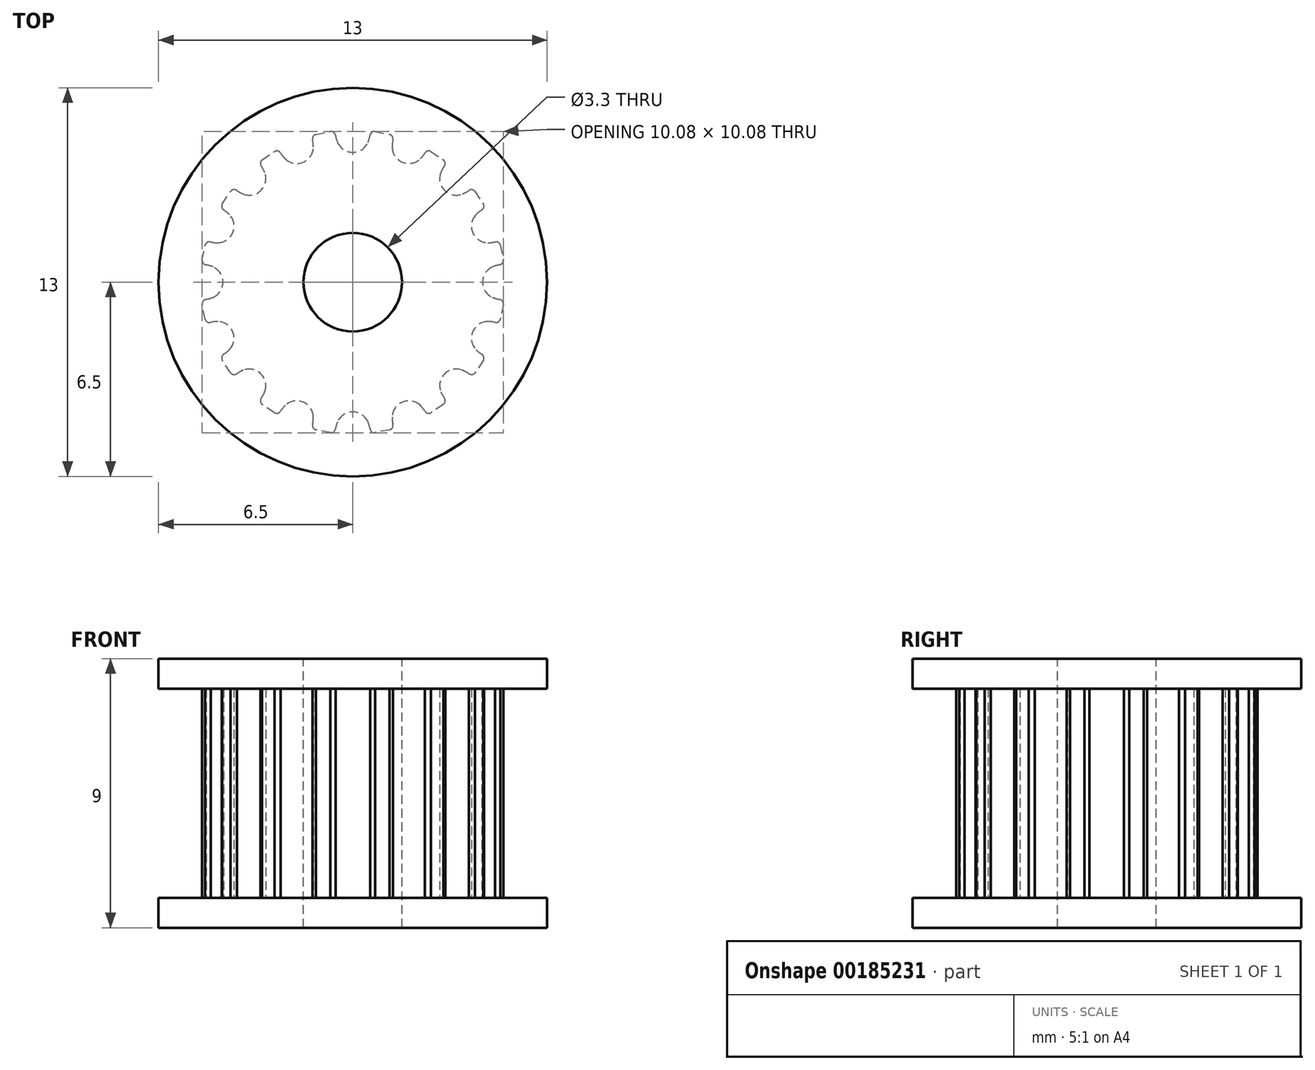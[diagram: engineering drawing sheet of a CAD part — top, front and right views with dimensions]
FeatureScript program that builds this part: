
annotation { "Feature Type Name" : "Feature", "Feature Type Description" : "" }
export const myFeature = defineFeature(function(context is Context, id is Id, definition is map)
    precondition{}
    {
        {
            var Q0;
            Q0=qCreatedBy(makeId("Top.planeOp"),FACE);
            var sketch = newSketch(context, id + "F0", { "sketchPlane" : qUnion([Q0])});
            skLineSegment(sketch, "E0", {"start": v(0, 0) * mm, "end": v(8.05, 0) * mm, "construction": true});
            skArc(sketch, "E1", {"start": v(5.1, 0) * mm, "mid": v(5, 1) * mm, "end": v(4.7, 1.95) * mm, "construction": true});
            skLineSegment(sketch, "E2", {"start": v(0, 0) * mm, "end": v(4.7, 1.95) * mm, "construction": true});
            skPoint(sketch, "E3", {"position": v(4.34, 0) * mm});
            skPoint(sketch, "E4", {"position": v(4.9, 0) * mm});
            skArc(sketch, "E5", {"start": v(4.68, 0.5) * mm, "mid": v(4.34, 0) * mm, "end": v(4.68, -0.5) * mm});
            skArc(sketch, "E6", {"start": v(4.9, 0.58) * mm, "mid": v(4.79, 0.55) * mm, "end": v(4.68, 0.5) * mm});
            skArc(sketch, "E7", {"start": v(4.94, 0) * mm, "mid": v(4.85, 0.96) * mm, "end": v(4.57, 1.9) * mm, "construction": true});
            skArc(sketch, "E8", {"start": v(4.9, 0.58) * mm, "mid": v(5, 0.64) * mm, "end": v(5.04, 0.75) * mm});
            skArc(sketch, "E9", {"start": v(4.97, -1.1) * mm, "mid": v(5.06, -0.56) * mm, "end": v(5.1, 0) * mm, "construction": true});
            skLineSegment(sketch, "E10", {"start": v(0, 0) * mm, "end": v(5, 1) * mm, "construction": true});
            skPoint(sketch, "E11", {"position": v(5, 1) * mm});
            skArc(sketch, "E12.MirrorCS", {"start": v(4.76, 1.34) * mm, "mid": v(4.87, 1.33) * mm, "end": v(4.94, 1.24) * mm});
            skArc(sketch, "E13.MirrorCS", {"start": v(4.76, 1.34) * mm, "mid": v(4.64, 1.32) * mm, "end": v(4.51, 1.32) * mm});
            skArc(sketch, "E14.MirrorCS", {"start": v(4.51, 1.32) * mm, "mid": v(4.01, 1.66) * mm, "end": v(4.12, 2.26) * mm});
            skLineSegment(sketch, "E15", {"start": v(4.94, 1.24) * mm, "end": v(5.04, 0.75) * mm});
            skArc(sketch, "E16.1.0", {"start": v(4.12, 2.26) * mm, "mid": v(4.01, 1.66) * mm, "end": v(4.51, 1.32) * mm});
            skArc(sketch, "E16.1.1", {"start": v(4.31, 2.41) * mm, "mid": v(4.21, 2.34) * mm, "end": v(4.12, 2.26) * mm});
            skArc(sketch, "E16.1.2", {"start": v(4.31, 2.41) * mm, "mid": v(4.38, 2.5) * mm, "end": v(4.37, 2.62) * mm});
            skLineSegment(sketch, "E16.1.3", {"start": v(4.1, 3.03) * mm, "end": v(4.37, 2.62) * mm});
            skArc(sketch, "E16.1.4", {"start": v(3.88, 3.06) * mm, "mid": v(4, 3.1) * mm, "end": v(4.1, 3.03) * mm});
            skArc(sketch, "E16.1.5", {"start": v(3.88, 3.06) * mm, "mid": v(3.78, 3) * mm, "end": v(3.67, 2.95) * mm});
            skArc(sketch, "E16.2.0", {"start": v(2.95, 3.67) * mm, "mid": v(3.07, 3.07) * mm, "end": v(3.67, 2.95) * mm});
            skArc(sketch, "E16.2.1", {"start": v(3.06, 3.88) * mm, "mid": v(3, 3.78) * mm, "end": v(2.95, 3.67) * mm});
            skArc(sketch, "E16.2.2", {"start": v(3.06, 3.88) * mm, "mid": v(3.1, 4) * mm, "end": v(3.03, 4.1) * mm});
            skLineSegment(sketch, "E16.2.3", {"start": v(2.62, 4.37) * mm, "end": v(3.03, 4.1) * mm});
            skArc(sketch, "E16.2.4", {"start": v(2.41, 4.31) * mm, "mid": v(2.5, 4.38) * mm, "end": v(2.62, 4.37) * mm});
            skArc(sketch, "E16.2.5", {"start": v(2.41, 4.31) * mm, "mid": v(2.34, 4.21) * mm, "end": v(2.26, 4.12) * mm});
            skArc(sketch, "E16.3.0", {"start": v(1.32, 4.51) * mm, "mid": v(1.66, 4.01) * mm, "end": v(2.26, 4.12) * mm});
            skArc(sketch, "E16.3.1", {"start": v(1.34, 4.76) * mm, "mid": v(1.32, 4.64) * mm, "end": v(1.32, 4.51) * mm});
            skArc(sketch, "E16.3.2", {"start": v(1.34, 4.76) * mm, "mid": v(1.33, 4.87) * mm, "end": v(1.24, 4.94) * mm});
            skLineSegment(sketch, "E16.3.3", {"start": v(0.75, 5.04) * mm, "end": v(1.24, 4.94) * mm});
            skArc(sketch, "E16.3.4", {"start": v(0.58, 4.9) * mm, "mid": v(0.64, 5) * mm, "end": v(0.75, 5.04) * mm});
            skArc(sketch, "E16.3.5", {"start": v(0.58, 4.9) * mm, "mid": v(0.55, 4.79) * mm, "end": v(0.5, 4.68) * mm});
            skArc(sketch, "E16.4.0", {"start": v(-0.5, 4.68) * mm, "mid": v(0, 4.34) * mm, "end": v(0.5, 4.68) * mm});
            skArc(sketch, "E16.4.1", {"start": v(-0.58, 4.9) * mm, "mid": v(-0.55, 4.79) * mm, "end": v(-0.5, 4.68) * mm});
            skArc(sketch, "E16.4.2", {"start": v(-0.58, 4.9) * mm, "mid": v(-0.64, 5) * mm, "end": v(-0.75, 5.04) * mm});
            skLineSegment(sketch, "E16.4.3", {"start": v(-1.24, 4.94) * mm, "end": v(-0.75, 5.04) * mm});
            skArc(sketch, "E16.4.4", {"start": v(-1.34, 4.76) * mm, "mid": v(-1.33, 4.87) * mm, "end": v(-1.24, 4.94) * mm});
            skArc(sketch, "E16.4.5", {"start": v(-1.34, 4.76) * mm, "mid": v(-1.32, 4.64) * mm, "end": v(-1.32, 4.51) * mm});
            skArc(sketch, "E16.5.0", {"start": v(-2.26, 4.12) * mm, "mid": v(-1.66, 4.01) * mm, "end": v(-1.32, 4.51) * mm});
            skArc(sketch, "E16.5.1", {"start": v(-2.41, 4.31) * mm, "mid": v(-2.34, 4.21) * mm, "end": v(-2.26, 4.12) * mm});
            skArc(sketch, "E16.5.2", {"start": v(-2.41, 4.31) * mm, "mid": v(-2.5, 4.38) * mm, "end": v(-2.62, 4.37) * mm});
            skLineSegment(sketch, "E16.5.3", {"start": v(-3.03, 4.1) * mm, "end": v(-2.62, 4.37) * mm});
            skArc(sketch, "E16.5.4", {"start": v(-3.06, 3.88) * mm, "mid": v(-3.1, 4) * mm, "end": v(-3.03, 4.1) * mm});
            skArc(sketch, "E16.5.5", {"start": v(-3.06, 3.88) * mm, "mid": v(-3, 3.78) * mm, "end": v(-2.95, 3.67) * mm});
            skArc(sketch, "E16.6.0", {"start": v(-3.67, 2.95) * mm, "mid": v(-3.07, 3.07) * mm, "end": v(-2.95, 3.67) * mm});
            skArc(sketch, "E16.6.1", {"start": v(-3.88, 3.06) * mm, "mid": v(-3.78, 3) * mm, "end": v(-3.67, 2.95) * mm});
            skArc(sketch, "E16.6.2", {"start": v(-3.88, 3.06) * mm, "mid": v(-4, 3.1) * mm, "end": v(-4.1, 3.03) * mm});
            skLineSegment(sketch, "E16.6.3", {"start": v(-4.37, 2.62) * mm, "end": v(-4.1, 3.03) * mm});
            skArc(sketch, "E16.6.4", {"start": v(-4.31, 2.41) * mm, "mid": v(-4.38, 2.5) * mm, "end": v(-4.37, 2.62) * mm});
            skArc(sketch, "E16.6.5", {"start": v(-4.31, 2.41) * mm, "mid": v(-4.21, 2.34) * mm, "end": v(-4.12, 2.26) * mm});
            skArc(sketch, "E16.7.0", {"start": v(-4.51, 1.32) * mm, "mid": v(-4.01, 1.66) * mm, "end": v(-4.12, 2.26) * mm});
            skArc(sketch, "E16.7.1", {"start": v(-4.76, 1.34) * mm, "mid": v(-4.64, 1.32) * mm, "end": v(-4.51, 1.32) * mm});
            skArc(sketch, "E16.7.2", {"start": v(-4.76, 1.34) * mm, "mid": v(-4.87, 1.33) * mm, "end": v(-4.94, 1.24) * mm});
            skLineSegment(sketch, "E16.7.3", {"start": v(-5.04, 0.75) * mm, "end": v(-4.94, 1.24) * mm});
            skArc(sketch, "E16.7.4", {"start": v(-4.9, 0.58) * mm, "mid": v(-5, 0.64) * mm, "end": v(-5.04, 0.75) * mm});
            skArc(sketch, "E16.7.5", {"start": v(-4.9, 0.58) * mm, "mid": v(-4.79, 0.55) * mm, "end": v(-4.68, 0.5) * mm});
            skArc(sketch, "E16.8.0", {"start": v(-4.68, -0.5) * mm, "mid": v(-4.34, 0) * mm, "end": v(-4.68, 0.5) * mm});
            skArc(sketch, "E16.8.1", {"start": v(-4.9, -0.58) * mm, "mid": v(-4.79, -0.55) * mm, "end": v(-4.68, -0.5) * mm});
            skArc(sketch, "E16.8.2", {"start": v(-4.9, -0.58) * mm, "mid": v(-5, -0.64) * mm, "end": v(-5.04, -0.75) * mm});
            skLineSegment(sketch, "E16.8.3", {"start": v(-4.94, -1.24) * mm, "end": v(-5.04, -0.75) * mm});
            skArc(sketch, "E16.8.4", {"start": v(-4.76, -1.34) * mm, "mid": v(-4.87, -1.33) * mm, "end": v(-4.94, -1.24) * mm});
            skArc(sketch, "E16.8.5", {"start": v(-4.76, -1.34) * mm, "mid": v(-4.64, -1.32) * mm, "end": v(-4.51, -1.32) * mm});
            skArc(sketch, "E16.9.0", {"start": v(-4.12, -2.26) * mm, "mid": v(-4.01, -1.66) * mm, "end": v(-4.51, -1.32) * mm});
            skArc(sketch, "E16.9.1", {"start": v(-4.31, -2.41) * mm, "mid": v(-4.21, -2.34) * mm, "end": v(-4.12, -2.26) * mm});
            skArc(sketch, "E16.9.2", {"start": v(-4.31, -2.41) * mm, "mid": v(-4.38, -2.5) * mm, "end": v(-4.37, -2.62) * mm});
            skLineSegment(sketch, "E16.9.3", {"start": v(-4.1, -3.03) * mm, "end": v(-4.37, -2.62) * mm});
            skArc(sketch, "E16.9.4", {"start": v(-3.88, -3.06) * mm, "mid": v(-4, -3.1) * mm, "end": v(-4.1, -3.03) * mm});
            skArc(sketch, "E16.9.5", {"start": v(-3.88, -3.06) * mm, "mid": v(-3.78, -3) * mm, "end": v(-3.67, -2.95) * mm});
            skArc(sketch, "E16.10.0", {"start": v(-2.95, -3.67) * mm, "mid": v(-3.07, -3.07) * mm, "end": v(-3.67, -2.95) * mm});
            skArc(sketch, "E16.10.1", {"start": v(-3.06, -3.88) * mm, "mid": v(-3, -3.78) * mm, "end": v(-2.95, -3.67) * mm});
            skArc(sketch, "E16.10.2", {"start": v(-3.06, -3.88) * mm, "mid": v(-3.1, -4) * mm, "end": v(-3.03, -4.1) * mm});
            skLineSegment(sketch, "E16.10.3", {"start": v(-2.62, -4.37) * mm, "end": v(-3.03, -4.1) * mm});
            skArc(sketch, "E16.10.4", {"start": v(-2.41, -4.31) * mm, "mid": v(-2.5, -4.38) * mm, "end": v(-2.62, -4.37) * mm});
            skArc(sketch, "E16.10.5", {"start": v(-2.41, -4.31) * mm, "mid": v(-2.34, -4.21) * mm, "end": v(-2.26, -4.12) * mm});
            skArc(sketch, "E16.11.0", {"start": v(-1.32, -4.51) * mm, "mid": v(-1.66, -4.01) * mm, "end": v(-2.26, -4.12) * mm});
            skArc(sketch, "E16.11.1", {"start": v(-1.34, -4.76) * mm, "mid": v(-1.32, -4.64) * mm, "end": v(-1.32, -4.51) * mm});
            skArc(sketch, "E16.11.2", {"start": v(-1.34, -4.76) * mm, "mid": v(-1.33, -4.87) * mm, "end": v(-1.24, -4.94) * mm});
            skLineSegment(sketch, "E16.11.3", {"start": v(-0.75, -5.04) * mm, "end": v(-1.24, -4.94) * mm});
            skArc(sketch, "E16.11.4", {"start": v(-0.58, -4.9) * mm, "mid": v(-0.64, -5) * mm, "end": v(-0.75, -5.04) * mm});
            skArc(sketch, "E16.11.5", {"start": v(-0.58, -4.9) * mm, "mid": v(-0.55, -4.79) * mm, "end": v(-0.5, -4.68) * mm});
            skArc(sketch, "E16.12.0", {"start": v(0.5, -4.68) * mm, "mid": v(0, -4.34) * mm, "end": v(-0.5, -4.68) * mm});
            skArc(sketch, "E16.12.1", {"start": v(0.58, -4.9) * mm, "mid": v(0.55, -4.79) * mm, "end": v(0.5, -4.68) * mm});
            skArc(sketch, "E16.12.2", {"start": v(0.58, -4.9) * mm, "mid": v(0.64, -5) * mm, "end": v(0.75, -5.04) * mm});
            skLineSegment(sketch, "E16.12.3", {"start": v(1.24, -4.94) * mm, "end": v(0.75, -5.04) * mm});
            skArc(sketch, "E16.12.4", {"start": v(1.34, -4.76) * mm, "mid": v(1.33, -4.87) * mm, "end": v(1.24, -4.94) * mm});
            skArc(sketch, "E16.12.5", {"start": v(1.34, -4.76) * mm, "mid": v(1.32, -4.64) * mm, "end": v(1.32, -4.51) * mm});
            skArc(sketch, "E16.13.0", {"start": v(2.26, -4.12) * mm, "mid": v(1.66, -4.01) * mm, "end": v(1.32, -4.51) * mm});
            skArc(sketch, "E16.13.1", {"start": v(2.41, -4.31) * mm, "mid": v(2.34, -4.21) * mm, "end": v(2.26, -4.12) * mm});
            skArc(sketch, "E16.13.2", {"start": v(2.41, -4.31) * mm, "mid": v(2.5, -4.38) * mm, "end": v(2.62, -4.37) * mm});
            skLineSegment(sketch, "E16.13.3", {"start": v(3.03, -4.1) * mm, "end": v(2.62, -4.37) * mm});
            skArc(sketch, "E16.13.4", {"start": v(3.06, -3.88) * mm, "mid": v(3.1, -4) * mm, "end": v(3.03, -4.1) * mm});
            skArc(sketch, "E16.13.5", {"start": v(3.06, -3.88) * mm, "mid": v(3, -3.78) * mm, "end": v(2.95, -3.67) * mm});
            skArc(sketch, "E16.14.0", {"start": v(3.67, -2.95) * mm, "mid": v(3.07, -3.07) * mm, "end": v(2.95, -3.67) * mm});
            skArc(sketch, "E16.14.1", {"start": v(3.88, -3.06) * mm, "mid": v(3.78, -3) * mm, "end": v(3.67, -2.95) * mm});
            skArc(sketch, "E16.14.2", {"start": v(3.88, -3.06) * mm, "mid": v(4, -3.1) * mm, "end": v(4.1, -3.03) * mm});
            skLineSegment(sketch, "E16.14.3", {"start": v(4.37, -2.62) * mm, "end": v(4.1, -3.03) * mm});
            skArc(sketch, "E16.14.4", {"start": v(4.31, -2.41) * mm, "mid": v(4.38, -2.5) * mm, "end": v(4.37, -2.62) * mm});
            skArc(sketch, "E16.14.5", {"start": v(4.31, -2.41) * mm, "mid": v(4.21, -2.34) * mm, "end": v(4.12, -2.26) * mm});
            skArc(sketch, "E16.15.0", {"start": v(4.51, -1.32) * mm, "mid": v(4.01, -1.66) * mm, "end": v(4.12, -2.26) * mm});
            skArc(sketch, "E16.15.1", {"start": v(4.76, -1.34) * mm, "mid": v(4.64, -1.32) * mm, "end": v(4.51, -1.32) * mm});
            skArc(sketch, "E16.15.2", {"start": v(4.76, -1.34) * mm, "mid": v(4.87, -1.33) * mm, "end": v(4.94, -1.24) * mm});
            skLineSegment(sketch, "E16.15.3", {"start": v(5.04, -0.75) * mm, "end": v(4.94, -1.24) * mm});
            skArc(sketch, "E16.15.4", {"start": v(4.9, -0.58) * mm, "mid": v(5, -0.64) * mm, "end": v(5.04, -0.75) * mm});
            skArc(sketch, "E16.15.5", {"start": v(4.9, -0.58) * mm, "mid": v(4.79, -0.55) * mm, "end": v(4.68, -0.5) * mm});
            skCircle(sketch, "E17", {"center": v(0, 0) * mm, "radius": 1.65 * mm});
            skCircle(sketch, "E18", {"center": v(0, 0) * mm, "radius": 6.5 * mm});
            skSolve(sketch);
        }
        {
            var Q0;
            Q0=makeQuery(id+"F0.imprint","IMPRINT",FACE,{"disambiguationData":[TD([[makeQuery(id+"F0.imprint","IMPRINT",EDGE,{"derivedFrom":sQuery(id+"F0.wireOp",EDGE,"E5")}),-1.0]])]});
            var Q1;
            Q1=makeQuery(id+"F0.imprint","IMPRINT",FACE,{"disambiguationData":[TD([[makeQuery(id+"F0.imprint","IMPRINT",EDGE,{"derivedFrom":sQuery(id+"F0.wireOp",EDGE,"E5")}),1.0]])]});
            extrude(context, id + "F1", {"entities" : qUnion([Q0, Q1]), "oppositeDirection" : true, "depth" : 1 * mm});
        }
        {
            var Q0;
            Q0=makeQuery(id+"F0.imprint","IMPRINT",FACE,{"disambiguationData":[TD([[makeQuery(id+"F0.imprint","IMPRINT",EDGE,{"derivedFrom":sQuery(id+"F0.wireOp",EDGE,"E5")}),-1.0]])]});
            extrude(context, id + "F2", {"entities" : qUnion([Q0]), "operationType" : NewBodyOperationType.ADD, "depth" : 7 * mm});
        }
        {
            var Q0;
            Q0=makeQuery(id+"F0.imprint","IMPRINT",FACE,{"disambiguationData":[TD([[makeQuery(id+"F0.imprint","IMPRINT",EDGE,{"derivedFrom":sQuery(id+"F0.wireOp",EDGE,"E5")}),1.0]])]});
            var Q1;
            Q1=makeQuery(id+"F0.imprint","IMPRINT",FACE,{"disambiguationData":[TD([[makeQuery(id+"F0.imprint","IMPRINT",EDGE,{"derivedFrom":sQuery(id+"F0.wireOp",EDGE,"E5")}),-1.0]])]});
            var Q2;
            Q2=makeQuery(id+"F2.opExtrude","CAP_FACE",FACE,{"disambiguationData":[OSD([sQuery(id+"F0.wireOp",EDGE,"E5"),sQuery(id+"F0.wireOp",EDGE,"E6"),sQuery(id+"F0.wireOp",EDGE,"E8"),sQuery(id+"F0.wireOp",EDGE,"E12.MirrorCS"),sQuery(id+"F0.wireOp",EDGE,"E13.MirrorCS"),sQuery(id+"F0.wireOp",EDGE,"E15"),sQuery(id+"F0.wireOp",EDGE,"E16.1.0"),sQuery(id+"F0.wireOp",EDGE,"E16.1.1"),sQuery(id+"F0.wireOp",EDGE,"E16.1.2"),sQuery(id+"F0.wireOp",EDGE,"E16.1.3"),sQuery(id+"F0.wireOp",EDGE,"E16.1.4"),sQuery(id+"F0.wireOp",EDGE,"E16.1.5"),sQuery(id+"F0.wireOp",EDGE,"E16.2.0"),sQuery(id+"F0.wireOp",EDGE,"E16.2.1"),sQuery(id+"F0.wireOp",EDGE,"E16.2.2"),sQuery(id+"F0.wireOp",EDGE,"E16.2.3"),sQuery(id+"F0.wireOp",EDGE,"E16.2.4"),sQuery(id+"F0.wireOp",EDGE,"E16.2.5"),sQuery(id+"F0.wireOp",EDGE,"E16.3.0"),sQuery(id+"F0.wireOp",EDGE,"E16.3.1"),sQuery(id+"F0.wireOp",EDGE,"E16.3.2"),sQuery(id+"F0.wireOp",EDGE,"E16.3.3"),sQuery(id+"F0.wireOp",EDGE,"E16.3.4"),sQuery(id+"F0.wireOp",EDGE,"E16.3.5"),sQuery(id+"F0.wireOp",EDGE,"E16.4.0"),sQuery(id+"F0.wireOp",EDGE,"E16.4.1"),sQuery(id+"F0.wireOp",EDGE,"E16.4.2"),sQuery(id+"F0.wireOp",EDGE,"E16.4.3"),sQuery(id+"F0.wireOp",EDGE,"E16.4.4"),sQuery(id+"F0.wireOp",EDGE,"E16.4.5"),sQuery(id+"F0.wireOp",EDGE,"E16.5.0"),sQuery(id+"F0.wireOp",EDGE,"E16.5.1"),sQuery(id+"F0.wireOp",EDGE,"E16.5.2"),sQuery(id+"F0.wireOp",EDGE,"E16.5.3"),sQuery(id+"F0.wireOp",EDGE,"E16.5.4"),sQuery(id+"F0.wireOp",EDGE,"E16.5.5"),sQuery(id+"F0.wireOp",EDGE,"E16.6.0"),sQuery(id+"F0.wireOp",EDGE,"E16.6.1"),sQuery(id+"F0.wireOp",EDGE,"E16.6.2"),sQuery(id+"F0.wireOp",EDGE,"E16.6.3"),sQuery(id+"F0.wireOp",EDGE,"E16.6.4"),sQuery(id+"F0.wireOp",EDGE,"E16.6.5"),sQuery(id+"F0.wireOp",EDGE,"E16.7.0"),sQuery(id+"F0.wireOp",EDGE,"E16.7.1"),sQuery(id+"F0.wireOp",EDGE,"E16.7.2"),sQuery(id+"F0.wireOp",EDGE,"E16.7.3"),sQuery(id+"F0.wireOp",EDGE,"E16.7.4"),sQuery(id+"F0.wireOp",EDGE,"E16.7.5"),sQuery(id+"F0.wireOp",EDGE,"E16.8.0"),sQuery(id+"F0.wireOp",EDGE,"E16.8.1"),sQuery(id+"F0.wireOp",EDGE,"E16.8.2"),sQuery(id+"F0.wireOp",EDGE,"E16.8.3"),sQuery(id+"F0.wireOp",EDGE,"E16.8.4"),sQuery(id+"F0.wireOp",EDGE,"E16.8.5"),sQuery(id+"F0.wireOp",EDGE,"E16.9.0"),sQuery(id+"F0.wireOp",EDGE,"E16.9.1"),sQuery(id+"F0.wireOp",EDGE,"E16.9.2"),sQuery(id+"F0.wireOp",EDGE,"E16.9.3"),sQuery(id+"F0.wireOp",EDGE,"E16.9.4"),sQuery(id+"F0.wireOp",EDGE,"E16.9.5"),sQuery(id+"F0.wireOp",EDGE,"E16.10.0"),sQuery(id+"F0.wireOp",EDGE,"E16.10.1"),sQuery(id+"F0.wireOp",EDGE,"E16.10.2"),sQuery(id+"F0.wireOp",EDGE,"E16.10.3"),sQuery(id+"F0.wireOp",EDGE,"E16.10.4"),sQuery(id+"F0.wireOp",EDGE,"E16.10.5"),sQuery(id+"F0.wireOp",EDGE,"E16.11.0"),sQuery(id+"F0.wireOp",EDGE,"E16.11.1"),sQuery(id+"F0.wireOp",EDGE,"E16.11.2"),sQuery(id+"F0.wireOp",EDGE,"E16.11.3"),sQuery(id+"F0.wireOp",EDGE,"E16.11.4"),sQuery(id+"F0.wireOp",EDGE,"E16.11.5"),sQuery(id+"F0.wireOp",EDGE,"E16.12.0"),sQuery(id+"F0.wireOp",EDGE,"E16.12.1"),sQuery(id+"F0.wireOp",EDGE,"E16.12.2"),sQuery(id+"F0.wireOp",EDGE,"E16.12.3"),sQuery(id+"F0.wireOp",EDGE,"E16.12.4"),sQuery(id+"F0.wireOp",EDGE,"E16.12.5"),sQuery(id+"F0.wireOp",EDGE,"E16.13.0"),sQuery(id+"F0.wireOp",EDGE,"E16.13.1"),sQuery(id+"F0.wireOp",EDGE,"E16.13.2"),sQuery(id+"F0.wireOp",EDGE,"E16.13.3"),sQuery(id+"F0.wireOp",EDGE,"E16.13.4"),sQuery(id+"F0.wireOp",EDGE,"E16.13.5"),sQuery(id+"F0.wireOp",EDGE,"E16.14.0"),sQuery(id+"F0.wireOp",EDGE,"E16.14.1"),sQuery(id+"F0.wireOp",EDGE,"E16.14.2"),sQuery(id+"F0.wireOp",EDGE,"E16.14.3"),sQuery(id+"F0.wireOp",EDGE,"E16.14.4"),sQuery(id+"F0.wireOp",EDGE,"E16.14.5"),sQuery(id+"F0.wireOp",EDGE,"E16.15.0"),sQuery(id+"F0.wireOp",EDGE,"E16.15.1"),sQuery(id+"F0.wireOp",EDGE,"E16.15.2"),sQuery(id+"F0.wireOp",EDGE,"E16.15.3"),sQuery(id+"F0.wireOp",EDGE,"E16.15.4"),sQuery(id+"F0.wireOp",EDGE,"E16.15.5"),sQuery(id+"F0.wireOp",EDGE,"E17")])],"isStart":false});
            var Q3;
            Q3=makeQuery(id+"F2.opExtrude","CAP_FACE",FACE,{"disambiguationData":[OSD([sQuery(id+"F0.wireOp",EDGE,"E5"),sQuery(id+"F0.wireOp",EDGE,"E6"),sQuery(id+"F0.wireOp",EDGE,"E8"),sQuery(id+"F0.wireOp",EDGE,"E12.MirrorCS"),sQuery(id+"F0.wireOp",EDGE,"E13.MirrorCS"),sQuery(id+"F0.wireOp",EDGE,"E15"),sQuery(id+"F0.wireOp",EDGE,"E16.1.0"),sQuery(id+"F0.wireOp",EDGE,"E16.1.1"),sQuery(id+"F0.wireOp",EDGE,"E16.1.2"),sQuery(id+"F0.wireOp",EDGE,"E16.1.3"),sQuery(id+"F0.wireOp",EDGE,"E16.1.4"),sQuery(id+"F0.wireOp",EDGE,"E16.1.5"),sQuery(id+"F0.wireOp",EDGE,"E16.2.0"),sQuery(id+"F0.wireOp",EDGE,"E16.2.1"),sQuery(id+"F0.wireOp",EDGE,"E16.2.2"),sQuery(id+"F0.wireOp",EDGE,"E16.2.3"),sQuery(id+"F0.wireOp",EDGE,"E16.2.4"),sQuery(id+"F0.wireOp",EDGE,"E16.2.5"),sQuery(id+"F0.wireOp",EDGE,"E16.3.0"),sQuery(id+"F0.wireOp",EDGE,"E16.3.1"),sQuery(id+"F0.wireOp",EDGE,"E16.3.2"),sQuery(id+"F0.wireOp",EDGE,"E16.3.3"),sQuery(id+"F0.wireOp",EDGE,"E16.3.4"),sQuery(id+"F0.wireOp",EDGE,"E16.3.5"),sQuery(id+"F0.wireOp",EDGE,"E16.4.0"),sQuery(id+"F0.wireOp",EDGE,"E16.4.1"),sQuery(id+"F0.wireOp",EDGE,"E16.4.2"),sQuery(id+"F0.wireOp",EDGE,"E16.4.3"),sQuery(id+"F0.wireOp",EDGE,"E16.4.4"),sQuery(id+"F0.wireOp",EDGE,"E16.4.5"),sQuery(id+"F0.wireOp",EDGE,"E16.5.0"),sQuery(id+"F0.wireOp",EDGE,"E16.5.1"),sQuery(id+"F0.wireOp",EDGE,"E16.5.2"),sQuery(id+"F0.wireOp",EDGE,"E16.5.3"),sQuery(id+"F0.wireOp",EDGE,"E16.5.4"),sQuery(id+"F0.wireOp",EDGE,"E16.5.5"),sQuery(id+"F0.wireOp",EDGE,"E16.6.0"),sQuery(id+"F0.wireOp",EDGE,"E16.6.1"),sQuery(id+"F0.wireOp",EDGE,"E16.6.2"),sQuery(id+"F0.wireOp",EDGE,"E16.6.3"),sQuery(id+"F0.wireOp",EDGE,"E16.6.4"),sQuery(id+"F0.wireOp",EDGE,"E16.6.5"),sQuery(id+"F0.wireOp",EDGE,"E16.7.0"),sQuery(id+"F0.wireOp",EDGE,"E16.7.1"),sQuery(id+"F0.wireOp",EDGE,"E16.7.2"),sQuery(id+"F0.wireOp",EDGE,"E16.7.3"),sQuery(id+"F0.wireOp",EDGE,"E16.7.4"),sQuery(id+"F0.wireOp",EDGE,"E16.7.5"),sQuery(id+"F0.wireOp",EDGE,"E16.8.0"),sQuery(id+"F0.wireOp",EDGE,"E16.8.1"),sQuery(id+"F0.wireOp",EDGE,"E16.8.2"),sQuery(id+"F0.wireOp",EDGE,"E16.8.3"),sQuery(id+"F0.wireOp",EDGE,"E16.8.4"),sQuery(id+"F0.wireOp",EDGE,"E16.8.5"),sQuery(id+"F0.wireOp",EDGE,"E16.9.0"),sQuery(id+"F0.wireOp",EDGE,"E16.9.1"),sQuery(id+"F0.wireOp",EDGE,"E16.9.2"),sQuery(id+"F0.wireOp",EDGE,"E16.9.3"),sQuery(id+"F0.wireOp",EDGE,"E16.9.4"),sQuery(id+"F0.wireOp",EDGE,"E16.9.5"),sQuery(id+"F0.wireOp",EDGE,"E16.10.0"),sQuery(id+"F0.wireOp",EDGE,"E16.10.1"),sQuery(id+"F0.wireOp",EDGE,"E16.10.2"),sQuery(id+"F0.wireOp",EDGE,"E16.10.3"),sQuery(id+"F0.wireOp",EDGE,"E16.10.4"),sQuery(id+"F0.wireOp",EDGE,"E16.10.5"),sQuery(id+"F0.wireOp",EDGE,"E16.11.0"),sQuery(id+"F0.wireOp",EDGE,"E16.11.1"),sQuery(id+"F0.wireOp",EDGE,"E16.11.2"),sQuery(id+"F0.wireOp",EDGE,"E16.11.3"),sQuery(id+"F0.wireOp",EDGE,"E16.11.4"),sQuery(id+"F0.wireOp",EDGE,"E16.11.5"),sQuery(id+"F0.wireOp",EDGE,"E16.12.0"),sQuery(id+"F0.wireOp",EDGE,"E16.12.1"),sQuery(id+"F0.wireOp",EDGE,"E16.12.2"),sQuery(id+"F0.wireOp",EDGE,"E16.12.3"),sQuery(id+"F0.wireOp",EDGE,"E16.12.4"),sQuery(id+"F0.wireOp",EDGE,"E16.12.5"),sQuery(id+"F0.wireOp",EDGE,"E16.13.0"),sQuery(id+"F0.wireOp",EDGE,"E16.13.1"),sQuery(id+"F0.wireOp",EDGE,"E16.13.2"),sQuery(id+"F0.wireOp",EDGE,"E16.13.3"),sQuery(id+"F0.wireOp",EDGE,"E16.13.4"),sQuery(id+"F0.wireOp",EDGE,"E16.13.5"),sQuery(id+"F0.wireOp",EDGE,"E16.14.0"),sQuery(id+"F0.wireOp",EDGE,"E16.14.1"),sQuery(id+"F0.wireOp",EDGE,"E16.14.2"),sQuery(id+"F0.wireOp",EDGE,"E16.14.3"),sQuery(id+"F0.wireOp",EDGE,"E16.14.4"),sQuery(id+"F0.wireOp",EDGE,"E16.14.5"),sQuery(id+"F0.wireOp",EDGE,"E16.15.0"),sQuery(id+"F0.wireOp",EDGE,"E16.15.1"),sQuery(id+"F0.wireOp",EDGE,"E16.15.2"),sQuery(id+"F0.wireOp",EDGE,"E16.15.3"),sQuery(id+"F0.wireOp",EDGE,"E16.15.4"),sQuery(id+"F0.wireOp",EDGE,"E16.15.5"),sQuery(id+"F0.wireOp",EDGE,"E17")])],"isStart":false});
            extrude(context, id + "F3", {"entities" : qUnion([Q0, Q1]), "operationType" : NewBodyOperationType.ADD, "endBoundEntityFace" : qUnion([Q2]), "depth" : 8 * mm, "hasSecondDirection" : true, "secondDirectionBound" : SecondDirectionBoundingType.UP_TO_SURFACE, "secondDirectionOppositeDirection" : false, "secondDirectionBoundEntityFace" : qUnion([Q3]), "secondDirectionDepth" : 8 * mm});
        }
    });
